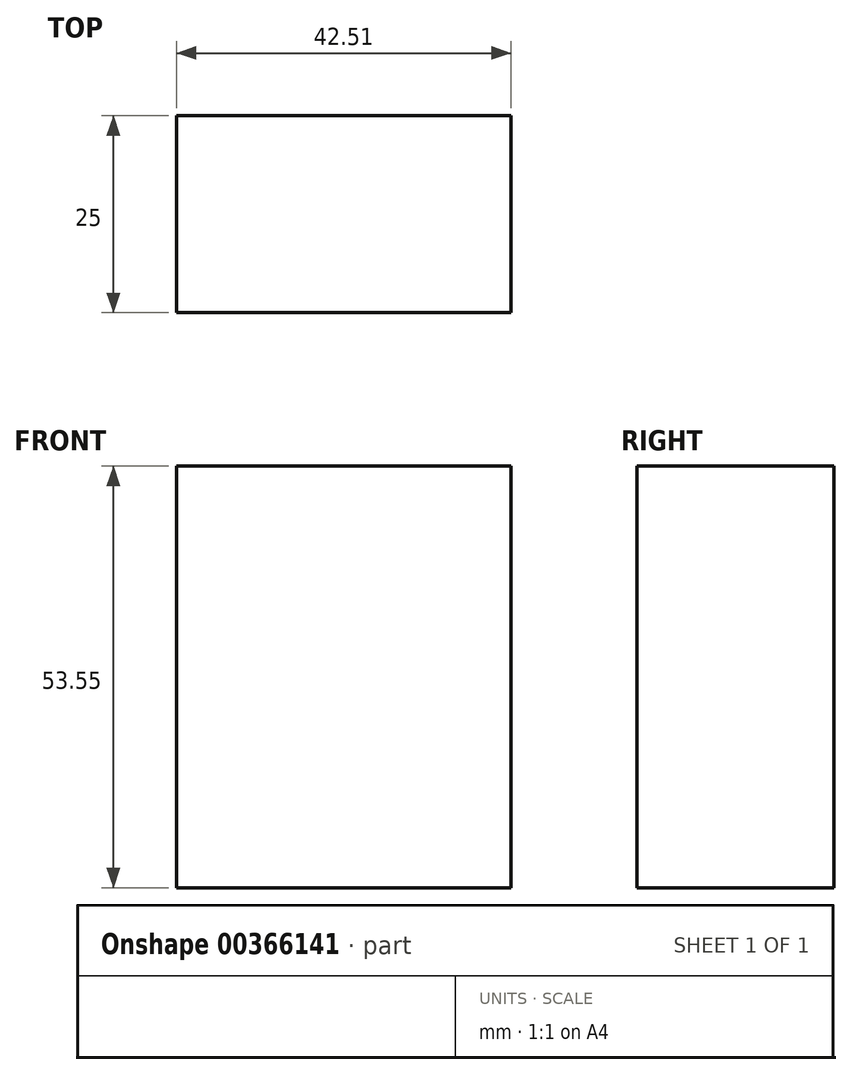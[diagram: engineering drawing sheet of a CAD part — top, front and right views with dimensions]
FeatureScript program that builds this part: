
annotation { "Feature Type Name" : "Feature", "Feature Type Description" : "" }
export const myFeature = defineFeature(function(context is Context, id is Id, definition is map)
    precondition{}
    {
        {
            var Q0;
            Q0=qCreatedBy(makeId("Front.planeOp"),FACE);
            var sketch = newSketch(context, id + "F0", { "sketchPlane" : qUnion([Q0])});
            skLineSegment(sketch, "E0.bottom", {"start": v(-74.4, 43.5) * mm, "end": v(-31.88, 43.5) * mm});
            skLineSegment(sketch, "E0.top", {"start": v(-74.4, -10.04) * mm, "end": v(-31.88, -10.04) * mm});
            skLineSegment(sketch, "E0.left", {"start": v(-74.4, 43.5) * mm, "end": v(-74.4, -10.04) * mm});
            skLineSegment(sketch, "E0.right", {"start": v(-31.88, 43.5) * mm, "end": v(-31.88, -10.04) * mm});
            skSolve(sketch);
        }
        {
            var Q0;
            Q0=makeQuery(id+"F0.imprint","IMPRINT",FACE,{"disambiguationData":[TD([[makeQuery(id+"F0.imprint","IMPRINT",EDGE,{"derivedFrom":sQuery(id+"F0.wireOp",EDGE,"E0.bottom")}),-1.0]])]});
            extrude(context, id + "F1", {"entities" : qUnion([Q0]), "depth" : 25 * mm});
        }
    });
